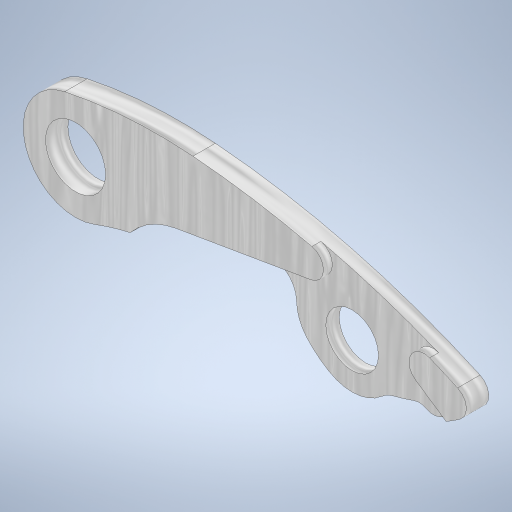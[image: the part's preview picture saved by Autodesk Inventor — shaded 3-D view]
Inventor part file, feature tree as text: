
AUTODESK INVENTOR PART (.ipt)
format: ipt  version: 2023 (Build 270158030, 158C)  size: 450,048 bytes
history: native  units: mm
features: sketch x2, extrude x2, projected_geometry x2
ambient origin geometry x8: Origin, YZ Plane, XZ Plane, XY Plane, X Axis, Y Axis, Z Axis, Center Point
bodies: Solid4 (feature_tree)
feature tree (6):
  sketch  "Sketch1"  dims[d1=8.05mm d2=6.0mm d3=14.0mm d4=60.0mm d5=35.0mm d8=22.0mm d10=12.0mm d11=7.05mm d12=20.0mm d13=14.05mm d15=0.1mm d16=30.0mm d17=5.0mm d18=2.0mm d19=106.0mm d21=21.118484mm d46=13.0mm]
  extrude  "Extrusion7"  Depth=106.0mm
  extrude  "Extrusion8"  Depth=12.0mm
  sketch  "Sketch4"  dims[d47=37.0mm d48=18.0mm d50=0.0mm d51=100.0mm d53=2.0mm d54=4.0mm d55=22.0mm d56=14.05mm d57=20.0mm d65=2.499311mm d68=4.604179mm d69=0.1mm d70=0.1mm d72=36.0mm d77=5.7mm d78=2.0mm d79=3.0mm d80=3.0mm d81=0.0mm d82=1.8mm d83=0.0mm d86=1.5mm d87=2.0mm d88=2.0mm d90=5.4mm d91=3.5mm d92=4.0mm d93=12.0mm d94=1.0mm d95=1.0mm d96=1.0mm d97=1.0mm]
  projected_geometry  "Projected Loop2"
  projected_geometry  "Projected Loop5"
